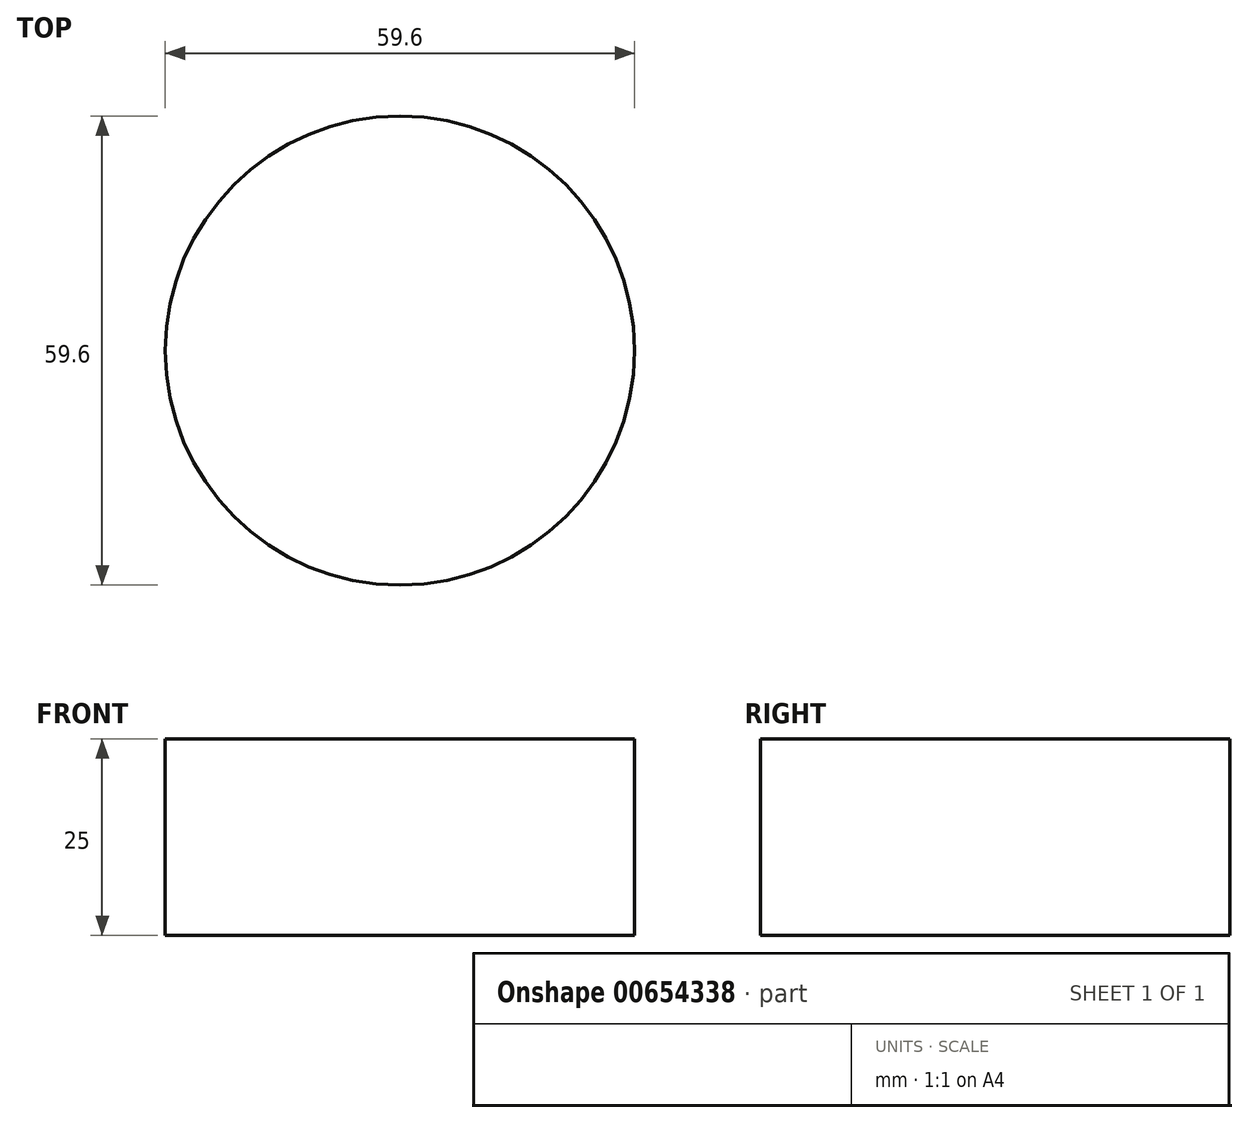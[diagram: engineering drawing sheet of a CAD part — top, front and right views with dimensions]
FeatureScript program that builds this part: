
annotation { "Feature Type Name" : "Feature", "Feature Type Description" : "" }
export const myFeature = defineFeature(function(context is Context, id is Id, definition is map)
    precondition{}
    {
        {
            var Q0;
            Q0=qCreatedBy(makeId("Top.planeOp"),FACE);
            var sketch = newSketch(context, id + "F0", { "sketchPlane" : qUnion([Q0])});
            skCircle(sketch, "E0", {"center": v(0, 0) * mm, "radius": 29.8 * mm});
            skSolve(sketch);
        }
        {
            var Q0;
            Q0=sQuery(id+"F0.wireOp",EDGE,"E0");
            extrude(context, id + "F1", {"bodyType" : ToolBodyType.SURFACE, "surfaceEntities" : qUnion([Q0]), "depth" : 25 * mm, "offsetDistance" : 25 * mm});
        }
    });
